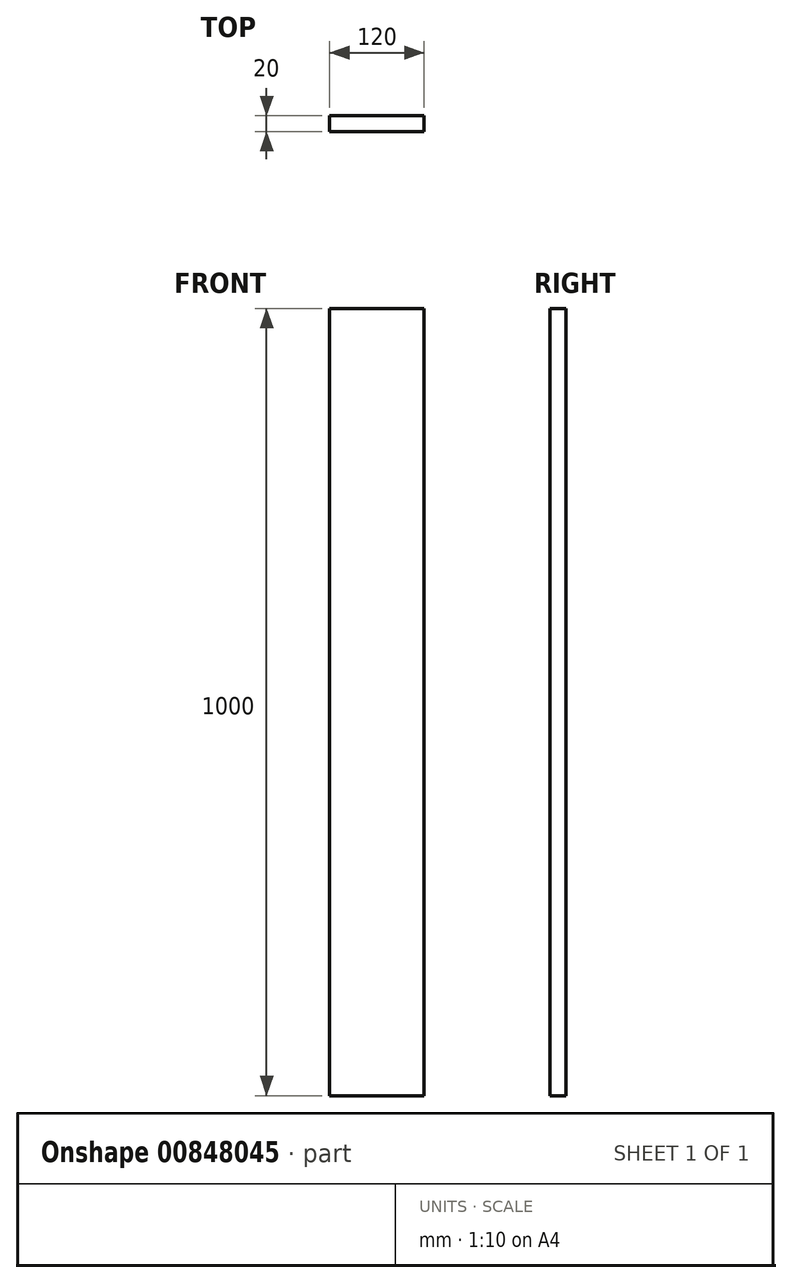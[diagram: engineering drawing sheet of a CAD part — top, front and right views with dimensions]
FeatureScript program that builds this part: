
annotation { "Feature Type Name" : "Feature", "Feature Type Description" : "" }
export const myFeature = defineFeature(function(context is Context, id is Id, definition is map)
    precondition{}
    {
        {
            var Q0;
            Q0=qCreatedBy(makeId("Top.planeOp"),FACE);
            var sketch = newSketch(context, id + "F0", { "sketchPlane" : qUnion([Q0])});
            skLineSegment(sketch, "E0.bottom", {"start": v(-99.45, 38.87) * mm, "end": v(20.55, 38.87) * mm});
            skLineSegment(sketch, "E0.top", {"start": v(-99.45, 18.87) * mm, "end": v(20.55, 18.87) * mm});
            skLineSegment(sketch, "E0.left", {"start": v(-99.45, 38.87) * mm, "end": v(-99.45, 18.87) * mm});
            skLineSegment(sketch, "E0.right", {"start": v(20.55, 38.87) * mm, "end": v(20.55, 18.87) * mm});
            skSolve(sketch);
        }
        {
            var Q0;
            Q0=makeQuery(id+"F0.imprint","IMPRINT",FACE,{"disambiguationData":[TD([[makeQuery(id+"F0.imprint","IMPRINT",EDGE,{"derivedFrom":sQuery(id+"F0.wireOp",EDGE,"E0.bottom")}),-1.0]])]});
            extrude(context, id + "F1", {"entities" : qUnion([Q0]), "depth" : 1000 * mm, "offsetDistance" : 25 * mm});
        }
    });
